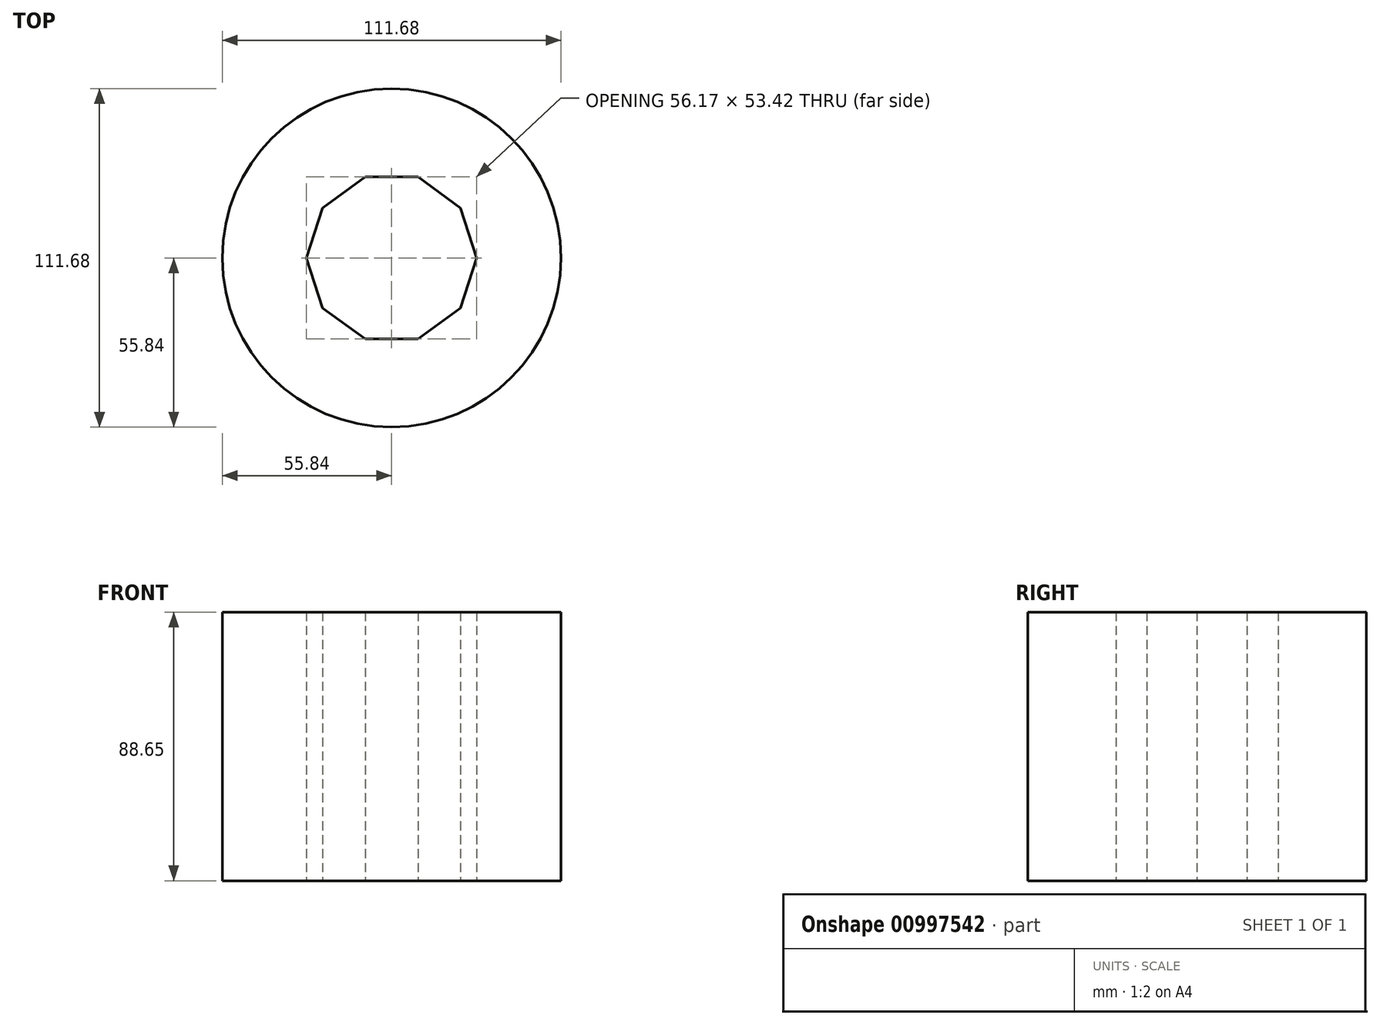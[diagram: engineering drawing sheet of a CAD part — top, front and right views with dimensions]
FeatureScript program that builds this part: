
annotation { "Feature Type Name" : "Feature", "Feature Type Description" : "" }
export const myFeature = defineFeature(function(context is Context, id is Id, definition is map)
    precondition{}
    {
        {
            var Q0;
            Q0=qCreatedBy(makeId("Top.planeOp"),FACE);
            var sketch = newSketch(context, id + "F0", { "sketchPlane" : qUnion([Q0])});
            skCircle(sketch, "E0", {"center": v(0, 0) * mm, "radius": 55.84 * mm});
            skSolve(sketch);
        }
        {
            var Q0;
            Q0 = qSketchRegion(id + "F0", true);
            extrude(context, id + "F1", {"entities" : qUnion([Q0]), "depth" : 88.65 * mm, "offsetDistance" : 25.4 * mm});
        }
        {
            var Q0;
            Q0=qCreatedBy(makeId("Top.planeOp"),FACE);
            var sketch = newSketch(context, id + "F2", { "sketchPlane" : qUnion([Q0])});
            skCircle(sketch, "E1.cCircle", {"center": v(0, 0) * mm, "radius": 26.71 * mm, "construction": true});
            skLineSegment(sketch, "E1.0", {"start": v(-8.68, 26.71) * mm, "end": v(8.68, 26.71) * mm});
            skLineSegment(sketch, "E1.1", {"start": v(8.68, 26.71) * mm, "end": v(22.72, 16.5) * mm});
            skLineSegment(sketch, "E1.2", {"start": v(22.72, 16.5) * mm, "end": v(28.09, 0) * mm});
            skLineSegment(sketch, "E1.3", {"start": v(28.09, 0) * mm, "end": v(22.72, -16.5) * mm});
            skLineSegment(sketch, "E1.4", {"start": v(22.72, -16.5) * mm, "end": v(8.68, -26.71) * mm});
            skLineSegment(sketch, "E1.5", {"start": v(8.68, -26.71) * mm, "end": v(-8.68, -26.71) * mm});
            skLineSegment(sketch, "E1.6", {"start": v(-8.68, -26.71) * mm, "end": v(-22.72, -16.5) * mm});
            skLineSegment(sketch, "E1.7", {"start": v(-22.72, -16.5) * mm, "end": v(-28.09, 0) * mm});
            skLineSegment(sketch, "E1.8", {"start": v(-28.09, 0) * mm, "end": v(-22.72, 16.5) * mm});
            skLineSegment(sketch, "E1.9", {"start": v(-22.72, 16.5) * mm, "end": v(-8.68, 26.71) * mm});
            skPoint(sketch, "E1.0.midPoint", {"position": v(0, 26.71) * mm});
            skSolve(sketch);
        }
        {
            var Q0;
            Q0 = qSketchRegion(id + "F2", true);
            extrude(context, id + "F3", {"entities" : qUnion([Q0]), "operationType" : NewBodyOperationType.REMOVE, "endBound" : BoundingType.THROUGH_ALL, "depth" : 25.4 * mm, "offsetDistance" : 25.4 * mm});
        }
    });
